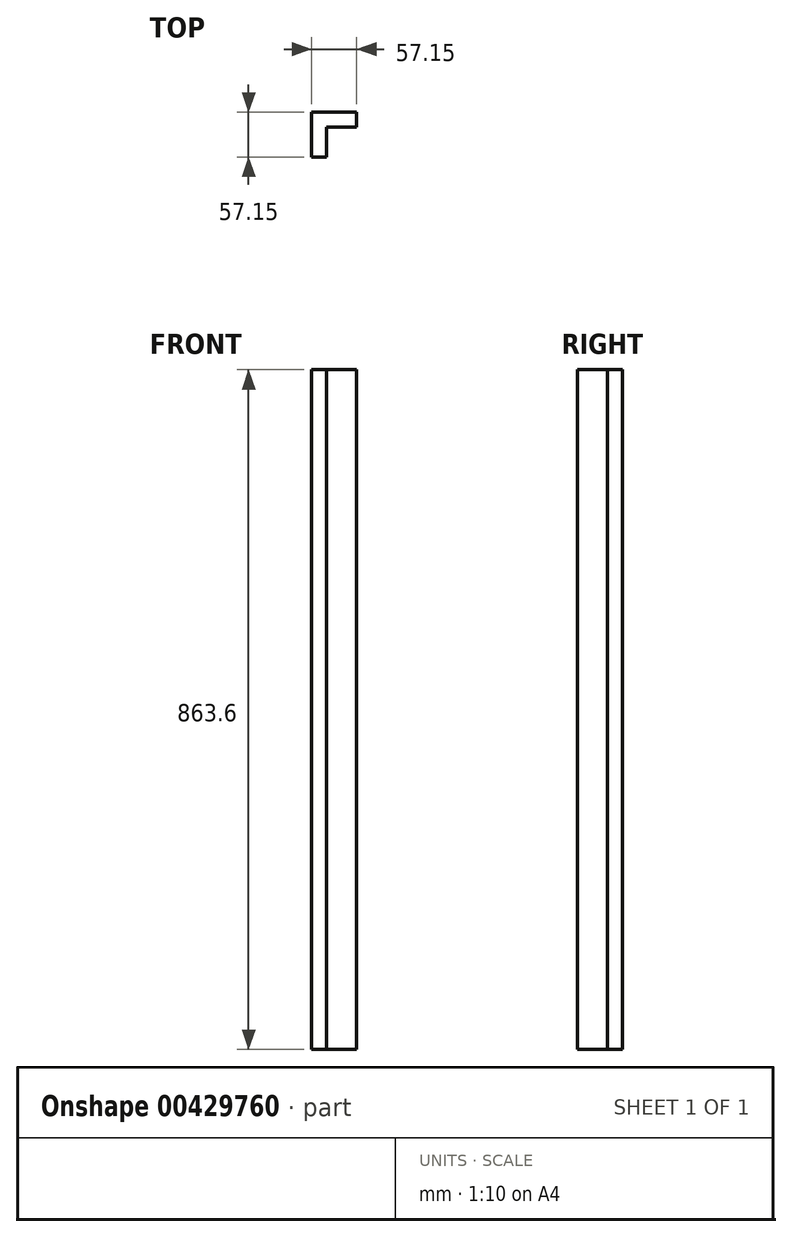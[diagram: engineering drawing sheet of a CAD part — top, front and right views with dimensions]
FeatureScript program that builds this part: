
annotation { "Feature Type Name" : "Feature", "Feature Type Description" : "" }
export const myFeature = defineFeature(function(context is Context, id is Id, definition is map)
    precondition{}
    {
        {
            var Q0;
            Q0=qCreatedBy(makeId("Top.planeOp"),FACE);
            var sketch = newSketch(context, id + "F0", { "sketchPlane" : qUnion([Q0])});
            skLineSegment(sketch, "E0", {"start": v(0, 0) * mm, "end": v(57.15, 0) * mm});
            skLineSegment(sketch, "E1", {"start": v(57.15, 0) * mm, "end": v(57.15, -19.05) * mm});
            skLineSegment(sketch, "E2", {"start": v(57.15, -19.05) * mm, "end": v(19.05, -19.05) * mm});
            skLineSegment(sketch, "E3", {"start": v(19.05, -19.05) * mm, "end": v(19.05, -57.15) * mm});
            skLineSegment(sketch, "E4", {"start": v(19.05, -57.15) * mm, "end": v(0, -57.15) * mm});
            skLineSegment(sketch, "E5", {"start": v(0, -57.15) * mm, "end": v(0, 0) * mm});
            skSolve(sketch);
        }
        {
            var Q0;
            Q0 = qSketchRegion(id + "F0", true);
            extrude(context, id + "F1", {"entities" : qUnion([Q0]), "depth" : 863.6 * mm});
        }
    });
